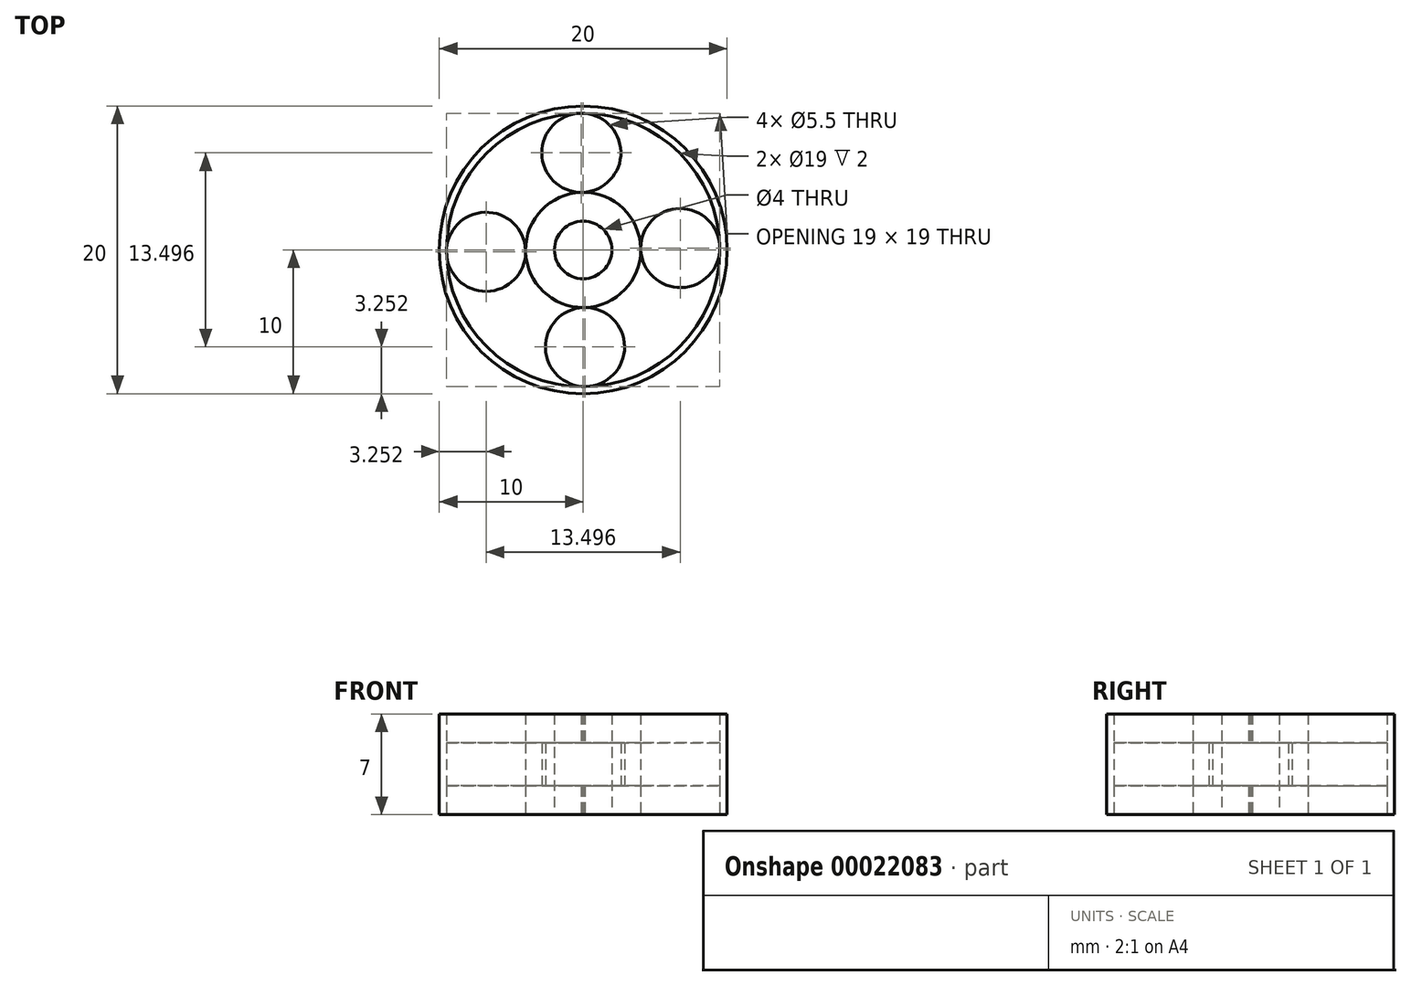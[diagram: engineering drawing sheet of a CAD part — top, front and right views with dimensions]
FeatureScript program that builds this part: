
annotation { "Feature Type Name" : "Feature", "Feature Type Description" : "" }
export const myFeature = defineFeature(function(context is Context, id is Id, definition is map)
    precondition{}
    {
        {
            var Q0;
            Q0=qCreatedBy(makeId("Top.planeOp"),FACE);
            var sketch = newSketch(context, id + "F0", { "sketchPlane" : qUnion([Q0])});
            skCircle(sketch, "E0", {"center": v(0, 0) * mm, "radius": 10 * mm});
            skPoint(sketch, "E1.orphan", {"position": v(-10, 0) * mm});
            skCircle(sketch, "E2", {"center": v(0, 0) * mm, "radius": 9.5 * mm});
            skCircle(sketch, "E3", {"center": v(0, 0) * mm, "radius": 4 * mm});
            skCircle(sketch, "E4", {"center": v(0, 0) * mm, "radius": 2 * mm});
            skCircle(sketch, "E5", {"center": v(-0.13, 6.75) * mm, "radius": 2.75 * mm});
            skCircle(sketch, "E6.1.0", {"center": v(-6.75, -0.13) * mm, "radius": 2.75 * mm});
            skCircle(sketch, "E6.2.0", {"center": v(0.13, -6.75) * mm, "radius": 2.75 * mm});
            skCircle(sketch, "E6.3.0", {"center": v(6.75, 0.13) * mm, "radius": 2.75 * mm});
            skSolve(sketch);
        }
        {
            var Q0;
            Q0=makeQuery(id+"F0.imprint","IMPRINT",FACE,{"disambiguationData":[TD([[makeQuery(id+"F0.imprint","IMPRINT",EDGE,{"derivedFrom":sQuery(id+"F0.wireOp",EDGE,"E0")}),1.0]])]});
            extrude(context, id + "F1", {"entities" : qUnion([Q0]), "endBound" : BoundingType.SYMMETRIC, "depth" : 7 * mm});
        }
        {
            var Q0;
            Q0=makeQuery(id+"F0.imprint","IMPRINT",FACE,{"disambiguationData":[TD([[makeQuery(id+"F0.imprint","IMPRINT",EDGE,{"derivedFrom":sQuery(id+"F0.wireOp",EDGE,"E2")}),1.0]])]});
            extrude(context, id + "F2", {"entities" : qUnion([Q0]), "operationType" : NewBodyOperationType.ADD, "endBound" : BoundingType.SYMMETRIC, "depth" : 3 * mm});
        }
        {
            var Q0;
            Q0=makeQuery(id+"F0.imprint","IMPRINT",FACE,{"disambiguationData":[TD([[makeQuery(id+"F0.imprint","IMPRINT",EDGE,{"derivedFrom":sQuery(id+"F0.wireOp",EDGE,"E4")}),-1.0]])]});
            extrude(context, id + "F3", {"entities" : qUnion([Q0]), "operationType" : NewBodyOperationType.ADD, "endBound" : BoundingType.SYMMETRIC, "depth" : 7 * mm});
        }
    });
